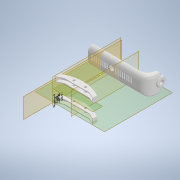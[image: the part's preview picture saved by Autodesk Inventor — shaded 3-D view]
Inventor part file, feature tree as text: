
AUTODESK INVENTOR PART (.ipt)
format: ipt  version: 2021 (Build 250183000, 183)  size: 755,712 bytes
history: native  units: mm
features: plane x9, sketch x8, mirror x5, extrude x4, sweep x1, fillet x1, projected_geometry x1, other x1
ambient origin geometry x8: Origin, YZ Plane, XZ Plane, XY Plane, X Axis, Y Axis, Z Axis, Center Point
bodies: Solid1 (feature_tree)
feature tree (30):
  sketch  "Sketch7"  dims[d10=10.0mm d11=31.4mm]
  plane  "Work Plane4"
  sketch  "Sketch8"  dims[d13=100.0mm d33=100.0mm]
  plane  "Work Plane5"
  plane  "Work Plane7"
  mirror  "Mirror4"
  sweep  "Sweep5"
  sketch  "Sketch15"  dims[d38=7.0mm d39=1.0mm]
  plane  "Work Plane13"
  extrude  "Extrusion7"  Depth=100.0mm
  mirror  "Mirror6"
  mirror  "Mirror7"
  extrude  "Extrusion8"  Depth=100.0mm
  plane  "Work Plane14"
  mirror  "Mirror8"
  mirror  "Mirror9"
  extrude  "Extrusion9"  Depth=1.0mm
  sketch  "Sketch18"  dims[d44=1.0mm]
  plane  "Work Plane15"
  plane  "Work Plane16"
  plane  "Work Plane17"
  extrude  "Extrusion11"  Depth=1.0mm
  fillet  "Fillet5"  Radius=9.0mm
  plane  "Work Plane9"
  sketch  "Sketch13"  dims[d36=100.0mm d37=100.0mm]
  projected_geometry  "Projected Loop5"
  sketch  "Sketch16"  dims[d40=9.0mm d41=1.0mm d42=9.0mm]
  sketch  "Sketch17"  dims[d43=3.5mm]
  sketch  "Sketch19"  dims[d45=3.5mm d46=1.0mm d47=1.0mm d48=5.0mm d49=1.0mm d50=5.0mm d71=0.0mm d72=0.0mm d75=1.0mm d76=0.0mm d77=1.0mm d78=0.0mm d79=3.0mm d80=3.0mm d81=38.5mm d82=0.0mm d85=2.0mm d86=2.0mm d87=0.0mm d88=0.0mm d89=2.0mm]
  other  "Cavity6"
